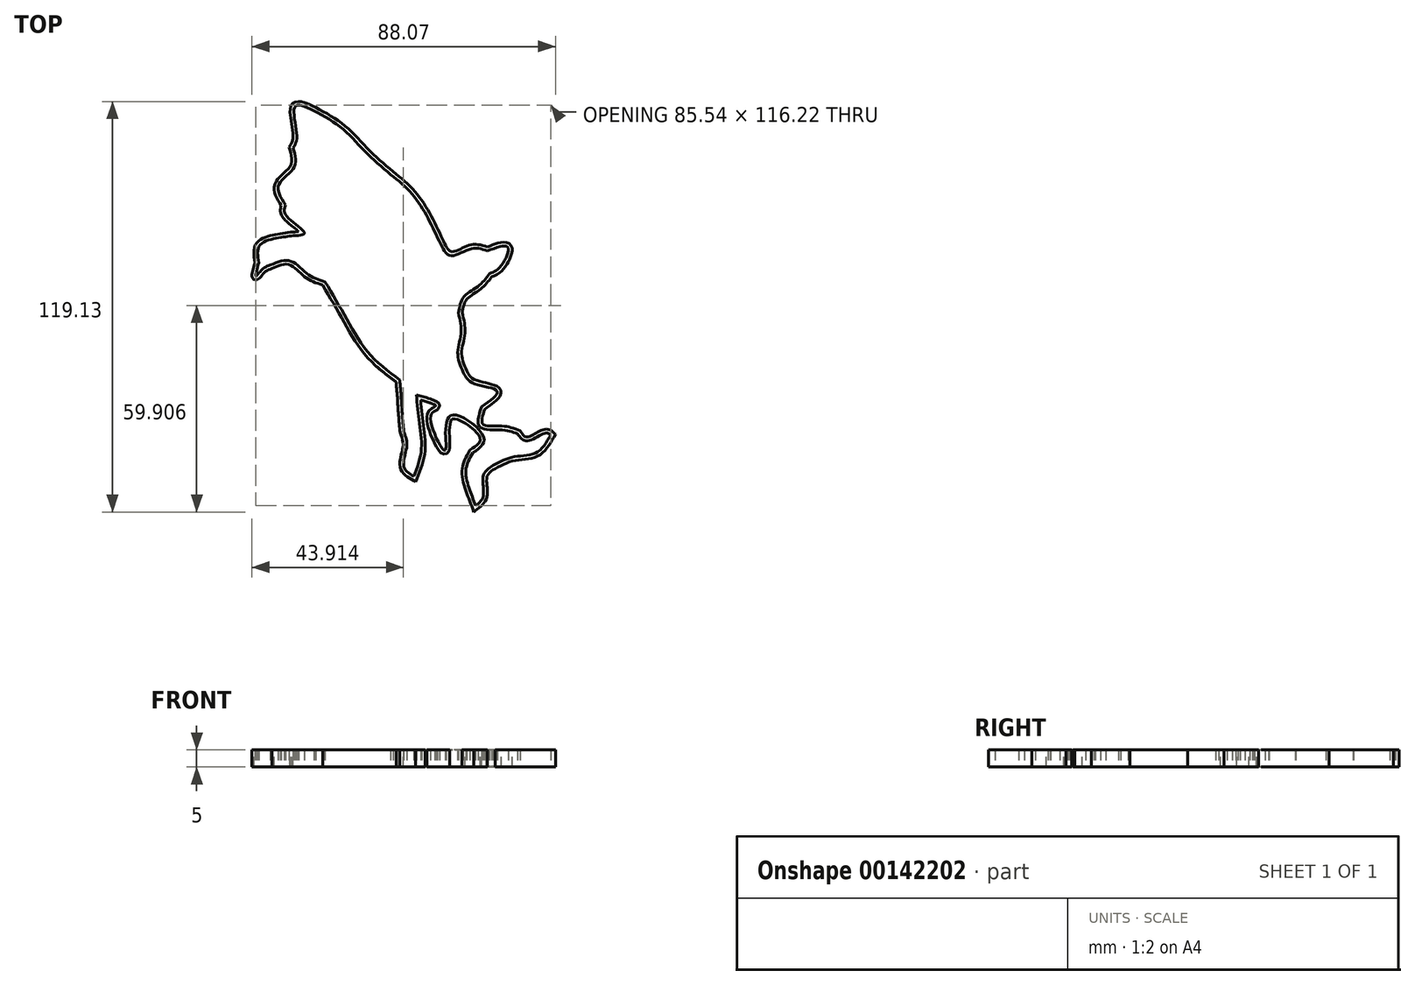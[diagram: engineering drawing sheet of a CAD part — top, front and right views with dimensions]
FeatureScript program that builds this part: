
annotation { "Feature Type Name" : "Feature", "Feature Type Description" : "" }
export const myFeature = defineFeature(function(context is Context, id is Id, definition is map)
    precondition{}
    {
        {
            var Q0;
            Q0=qCreatedBy(makeId("Top.planeOp"),FACE);
            var sketch = newSketch(context, id + "F0", { "sketchPlane" : qUnion([Q0])});
            skFitSpline(sketch, "E0", {"points": [v(103.2, -286.92) * mm, v(94.21, -262.34) * mm, v(89.17, -235.03) * mm, v(99.29, -209.97) * mm]});
            skFitSpline(sketch, "E1", {"points": [v(99.29, -209.97) * mm, v(115.29, -187.64) * mm, v(69.8, -155.06) * mm, v(59.57, -181.54) * mm]});
            skFitSpline(sketch, "E2", {"points": [v(59.57, -181.54) * mm, v(57.67, -206.47) * mm, v(37.89, -158.35) * mm, v(48.03, -147.78) * mm]});
            skFitSpline(sketch, "E3", {"points": [v(48.03, -147.78) * mm, v(49.04, -137.4) * mm, v(12.76, -124.9) * mm, v(17.28, -124.86) * mm]});
            skFitSpline(sketch, "E4", {"points": [v(17.28, -124.86) * mm, v(21.35, -164.45) * mm, v(24.6, -205.8) * mm, v(13.7, -244.38) * mm]});
            skFitSpline(sketch, "E5", {"points": [v(13.7, -244.38) * mm, v(-0.94, -229.56) * mm, v(3.45, -200.2) * mm, v(-0.8, -179.43) * mm]});
            skFitSpline(sketch, "E6", {"points": [v(-0.8, -179.43) * mm, v(-3.1, -154.44) * mm, v(-4.68, -129.38) * mm, v(-6.77, -104.36) * mm]});
            skFitSpline(sketch, "E7", {"points": [v(-6.77, -104.36) * mm, v(-52.26, -64.85) * mm, v(-85.04, -13.53) * mm, v(-115.1, 38.08) * mm]});
            skFitSpline(sketch, "E8", {"points": [v(-115.1, 38.08) * mm, v(-140.25, 49.12) * mm, v(-165.75, 68.34) * mm, v(-194.43, 62.4) * mm]});
            skFitSpline(sketch, "E9", {"points": [v(-194.43, 62.4) * mm, v(-207, 55.54) * mm, v(-215.34, 46.2) * mm, v(-211.21, 65.66) * mm]});
            skFitSpline(sketch, "E10", {"points": [v(-211.21, 65.66) * mm, v(-209.77, 91.2) * mm, v(-183, 101.89) * mm, v(-161.23, 104.87) * mm]});
            skFitSpline(sketch, "E11", {"points": [v(-161.23, 104.87) * mm, v(-145.1, 109.22) * mm, v(-171.94, 134.8) * mm, v(-172.6, 149.63) * mm]});
            skFitSpline(sketch, "E12", {"points": [v(-172.6, 149.63) * mm, v(-182.67, 178.21) * mm, v(-160.44, 203.7) * mm, v(-161.35, 232.56) * mm]});
            skFitSpline(sketch, "E13", {"points": [v(-161.35, 232.56) * mm, v(-156.06, 250.52) * mm, v(-158.72, 292.15) * mm, v(-131.4, 286.38) * mm]});
            skFitSpline(sketch, "E14", {"points": [v(-131.4, 286.38) * mm, v(-90.34, 260.57) * mm, v(-55.8, 225.88) * mm, v(-19.77, 193.73) * mm]});
            skFitSpline(sketch, "E15", {"points": [v(-19.77, 193.73) * mm, v(9.98, 166.86) * mm, v(32.74, 133.12) * mm, v(50.37, 97.38) * mm]});
            skFitSpline(sketch, "E16", {"points": [v(50.37, 97.38) * mm, v(67.05, 76.17) * mm, v(96.98, 86.08) * mm, v(120.1, 82.81) * mm]});
            skFitSpline(sketch, "E17", {"points": [v(120.1, 82.81) * mm, v(150.06, 88) * mm, v(139.48, 60.35) * mm, v(123.34, 50.04) * mm]});
            skFitSpline(sketch, "E18", {"points": [v(123.34, 50.04) * mm, v(107.41, 32.08) * mm, v(85.97, 15.9) * mm, v(78.24, -7.34) * mm]});
            skFitSpline(sketch, "E19", {"points": [v(78.24, -7.34) * mm, v(82.3, -35.87) * mm, v(77.35, -65.49) * mm, v(85.54, -93.4) * mm]});
            skFitSpline(sketch, "E20", {"points": [v(85.54, -93.4) * mm, v(99.56, -108.94) * mm, v(134.48, -120.66) * mm, v(111.79, -143.35) * mm]});
            skFitSpline(sketch, "E21", {"points": [v(111.79, -143.35) * mm, v(109.47, -172.63) * mm, v(142.67, -176.88) * mm, v(164.13, -182.53) * mm]});
            skFitSpline(sketch, "E22", {"points": [v(164.13, -182.53) * mm, v(178, -192.7) * mm, v(204.79, -181.24) * mm, v(212.27, -184.42) * mm]});
            skFitSpline(sketch, "E23", {"points": [v(212.27, -184.42) * mm, v(191.15, -209.75) * mm, v(157.56, -216.13) * mm, v(128.78, -228.37) * mm]});
            skFitSpline(sketch, "E24", {"points": [v(128.78, -228.37) * mm, v(114.54, -243.2) * mm, v(114.34, -272.73) * mm, v(103.2, -286.92) * mm]});
            skSolve(sketch);
        }
        {
            var Q0;
            Q0 = qSketchRegion(id + "F0", true);
            extrude(context, id + "F1", {"entities" : qUnion([Q0]), "depth" : 25 * mm});
        }
        {
            var Q0;
            Q0=makeQuery(id+"F1.opExtrude","SWEPT_BODY",BODY,{"disambiguationData":[OSD([sQuery(id+"F0.wireOp",EDGE,"E0"),sQuery(id+"F0.wireOp",EDGE,"E1"),sQuery(id+"F0.wireOp",EDGE,"E2"),sQuery(id+"F0.wireOp",EDGE,"E3"),sQuery(id+"F0.wireOp",EDGE,"E4"),sQuery(id+"F0.wireOp",EDGE,"E5"),sQuery(id+"F0.wireOp",EDGE,"E6"),sQuery(id+"F0.wireOp",EDGE,"E7"),sQuery(id+"F0.wireOp",EDGE,"E8"),sQuery(id+"F0.wireOp",EDGE,"E9"),sQuery(id+"F0.wireOp",EDGE,"E10"),sQuery(id+"F0.wireOp",EDGE,"E11"),sQuery(id+"F0.wireOp",EDGE,"E12"),sQuery(id+"F0.wireOp",EDGE,"E13"),sQuery(id+"F0.wireOp",EDGE,"E14"),sQuery(id+"F0.wireOp",EDGE,"E15"),sQuery(id+"F0.wireOp",EDGE,"E16"),sQuery(id+"F0.wireOp",EDGE,"E17"),sQuery(id+"F0.wireOp",EDGE,"E18"),sQuery(id+"F0.wireOp",EDGE,"E19"),sQuery(id+"F0.wireOp",EDGE,"E20"),sQuery(id+"F0.wireOp",EDGE,"E21"),sQuery(id+"F0.wireOp",EDGE,"E22"),sQuery(id+"F0.wireOp",EDGE,"E23"),sQuery(id+"F0.wireOp",EDGE,"E24")])]});
            var Q1;
            Q1=qCreatedBy(makeId("Origin.pointOp"),VERTEX);
            transform(context, id + "F2", {"entities" : qUnion([Q0]), "transformType" : TransformType.SCALE_UNIFORMLY, "scale" : 0.2, "scalePoint" : qUnion([Q1]), "makeCopy" : false});
        }
        {
            var Q0;
            Q0=makeQuery(id+"F1.opExtrude","CAP_FACE",FACE,{"disambiguationData":[OSD([sQuery(id+"F0.wireOp",EDGE,"E0"),sQuery(id+"F0.wireOp",EDGE,"E1"),sQuery(id+"F0.wireOp",EDGE,"E2"),sQuery(id+"F0.wireOp",EDGE,"E3"),sQuery(id+"F0.wireOp",EDGE,"E4"),sQuery(id+"F0.wireOp",EDGE,"E5"),sQuery(id+"F0.wireOp",EDGE,"E6"),sQuery(id+"F0.wireOp",EDGE,"E7"),sQuery(id+"F0.wireOp",EDGE,"E8"),sQuery(id+"F0.wireOp",EDGE,"E9"),sQuery(id+"F0.wireOp",EDGE,"E10"),sQuery(id+"F0.wireOp",EDGE,"E11"),sQuery(id+"F0.wireOp",EDGE,"E12"),sQuery(id+"F0.wireOp",EDGE,"E13"),sQuery(id+"F0.wireOp",EDGE,"E14"),sQuery(id+"F0.wireOp",EDGE,"E15"),sQuery(id+"F0.wireOp",EDGE,"E16"),sQuery(id+"F0.wireOp",EDGE,"E17"),sQuery(id+"F0.wireOp",EDGE,"E18"),sQuery(id+"F0.wireOp",EDGE,"E19"),sQuery(id+"F0.wireOp",EDGE,"E20"),sQuery(id+"F0.wireOp",EDGE,"E21"),sQuery(id+"F0.wireOp",EDGE,"E22"),sQuery(id+"F0.wireOp",EDGE,"E23"),sQuery(id+"F0.wireOp",EDGE,"E24")])],"isStart":false});
            var Q1;
            Q1=makeQuery(id+"F1.opExtrude","CAP_FACE",FACE,{"disambiguationData":[OSD([sQuery(id+"F0.wireOp",EDGE,"E0"),sQuery(id+"F0.wireOp",EDGE,"E1"),sQuery(id+"F0.wireOp",EDGE,"E2"),sQuery(id+"F0.wireOp",EDGE,"E3"),sQuery(id+"F0.wireOp",EDGE,"E4"),sQuery(id+"F0.wireOp",EDGE,"E5"),sQuery(id+"F0.wireOp",EDGE,"E6"),sQuery(id+"F0.wireOp",EDGE,"E7"),sQuery(id+"F0.wireOp",EDGE,"E8"),sQuery(id+"F0.wireOp",EDGE,"E9"),sQuery(id+"F0.wireOp",EDGE,"E10"),sQuery(id+"F0.wireOp",EDGE,"E11"),sQuery(id+"F0.wireOp",EDGE,"E12"),sQuery(id+"F0.wireOp",EDGE,"E13"),sQuery(id+"F0.wireOp",EDGE,"E14"),sQuery(id+"F0.wireOp",EDGE,"E15"),sQuery(id+"F0.wireOp",EDGE,"E16"),sQuery(id+"F0.wireOp",EDGE,"E17"),sQuery(id+"F0.wireOp",EDGE,"E18"),sQuery(id+"F0.wireOp",EDGE,"E19"),sQuery(id+"F0.wireOp",EDGE,"E20"),sQuery(id+"F0.wireOp",EDGE,"E21"),sQuery(id+"F0.wireOp",EDGE,"E22"),sQuery(id+"F0.wireOp",EDGE,"E23"),sQuery(id+"F0.wireOp",EDGE,"E24")])],"isStart":true});
            shell(context, id + "F3", {"entities" : qUnion([Q0, Q1]), "thickness" : 1.1 * mm, "oppositeDirection" : true});
        }
    });
